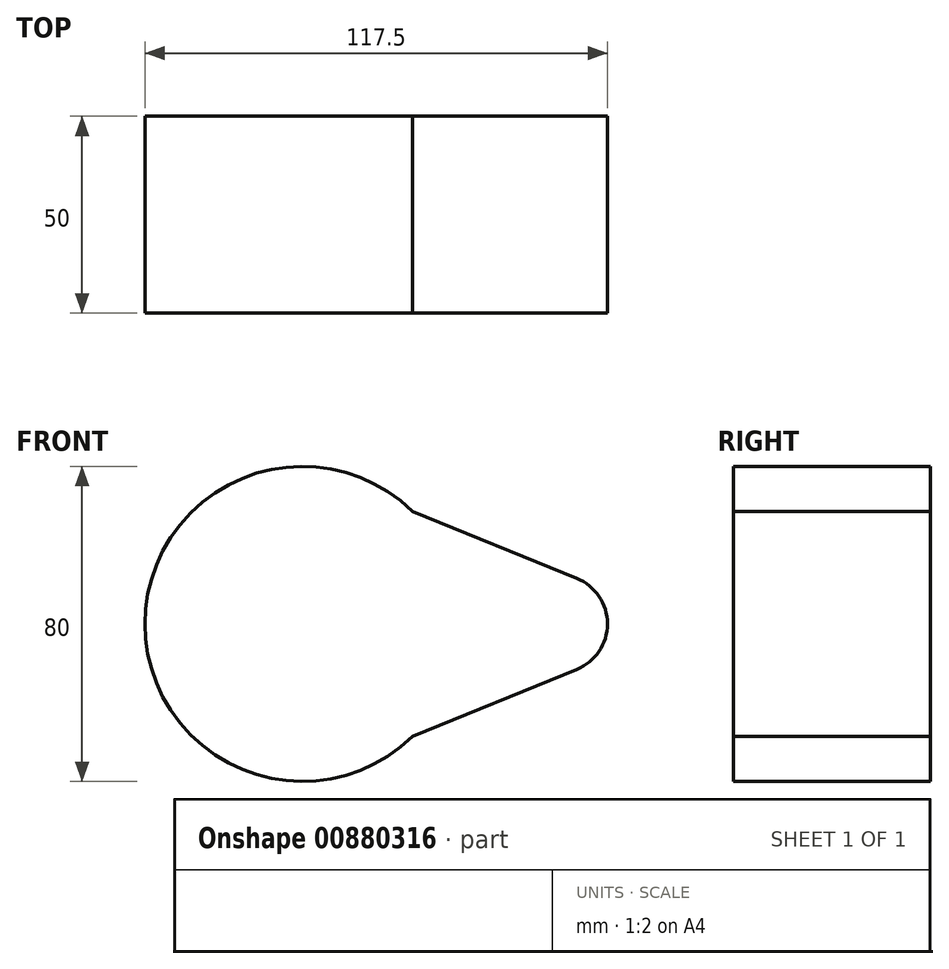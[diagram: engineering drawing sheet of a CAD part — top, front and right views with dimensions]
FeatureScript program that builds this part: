
annotation { "Feature Type Name" : "Feature", "Feature Type Description" : "" }
export const myFeature = defineFeature(function(context is Context, id is Id, definition is map)
    precondition{}
    {
        {
            var Q0;
            Q0=qCreatedBy(makeId("Front.planeOp"),FACE);
            var sketch = newSketch(context, id + "F0", { "sketchPlane" : qUnion([Q0])});
            skCircle(sketch, "E0", {"center": v(0, 0) * mm, "radius": 40 * mm});
            skCircle(sketch, "E1", {"center": v(65, 0) * mm, "radius": 12.5 * mm});
            skLineSegment(sketch, "E2", {"start": v(27.97, -28.6) * mm, "end": v(69.72, -11.57) * mm});
            skLineSegment(sketch, "E3", {"start": v(27.97, 28.6) * mm, "end": v(69.72, 11.57) * mm});
            skPoint(sketch, "E4.orphan", {"position": v(0, 40) * mm});
            skPoint(sketch, "E5.orphan", {"position": v(0, -40) * mm});
            skSolve(sketch);
        }
        {
            var Q0;
            Q0=qCreatedBy(makeId("Front.planeOp"),FACE);
            var sketch = newSketch(context, id + "F1", { "sketchPlane" : qUnion([Q0])});
            skCircle(sketch, "E6", {"center": v(0, 0) * mm, "radius": 6 * mm});
            skCircle(sketch, "E7", {"center": v(64.78, 0) * mm, "radius": 6 * mm});
            skSolve(sketch);
        }
        {
            var Q0;
            {var subQ0=sQuery(id+"F0.wireOp",EDGE,"E0");var subQ1=makeQuery(id+"F0.imprint","INTERSECT",VERTEX,{"derivedFrom":[subQ0,sQuery(id+"F0.wireOp",EDGE,"E2")]});Q0=makeQuery(id+"F0.imprint","IMPRINT",FACE,{"disambiguationData":[TD([[makeQuery(id+"F0.imprint","IMPRINT",EDGE,{"disambiguationData":[TD([[subQ1,1.0]])],"derivedFrom":subQ0}),1.0]])]});}
            var Q1;
            {var subQ0=sQuery(id+"F0.wireOp",EDGE,"E1");var subQ1=makeQuery(id+"F0.imprint","INTERSECT",VERTEX,{"derivedFrom":[subQ0,sQuery(id+"F0.wireOp",EDGE,"E2")]});Q1=makeQuery(id+"F0.imprint","IMPRINT",FACE,{"disambiguationData":[TD([[makeQuery(id+"F0.imprint","IMPRINT",EDGE,{"disambiguationData":[TD([[subQ1,1.0]])],"derivedFrom":subQ0}),1.0]])]});}
            var Q2;
            {var subQ0=sQuery(id+"F0.wireOp",EDGE,"E2");Q2=makeQuery(id+"F0.imprint","IMPRINT",FACE,{"disambiguationData":[TD([[makeQuery(id+"F0.imprint","IMPRINT",EDGE,{"derivedFrom":subQ0}),1.0]])]});}
            extrude(context, id + "F2", {"entities" : qUnion([Q0, Q1, Q2]), "depth" : 25 * mm, "offsetDistance" : 25 * mm});
        }
        {
            var Q0;
            Q0=makeQuery(id+"F2.opExtrude","CAP_FACE",FACE,{"disambiguationData":[OSD([sQuery(id+"F0.wireOp",EDGE,"E0"),sQuery(id+"F0.wireOp",EDGE,"E1"),sQuery(id+"F0.wireOp",EDGE,"E2"),sQuery(id+"F0.wireOp",EDGE,"E3")])],"isStart":false});
            extrude(context, id + "F3", {"entities" : qUnion([Q0]), "operationType" : NewBodyOperationType.ADD, "depth" : 25 * mm, "offsetDistance" : 25 * mm});
        }
        {
            var Q0;
            Q0 = qSketchRegion(id + "F1", true);
            extrude(context, id + "F4", {"entities" : qUnion([Q0]), "operationType" : NewBodyOperationType.ADD, "depth" : 50 * mm, "offsetDistance" : 25 * mm});
        }
    });
